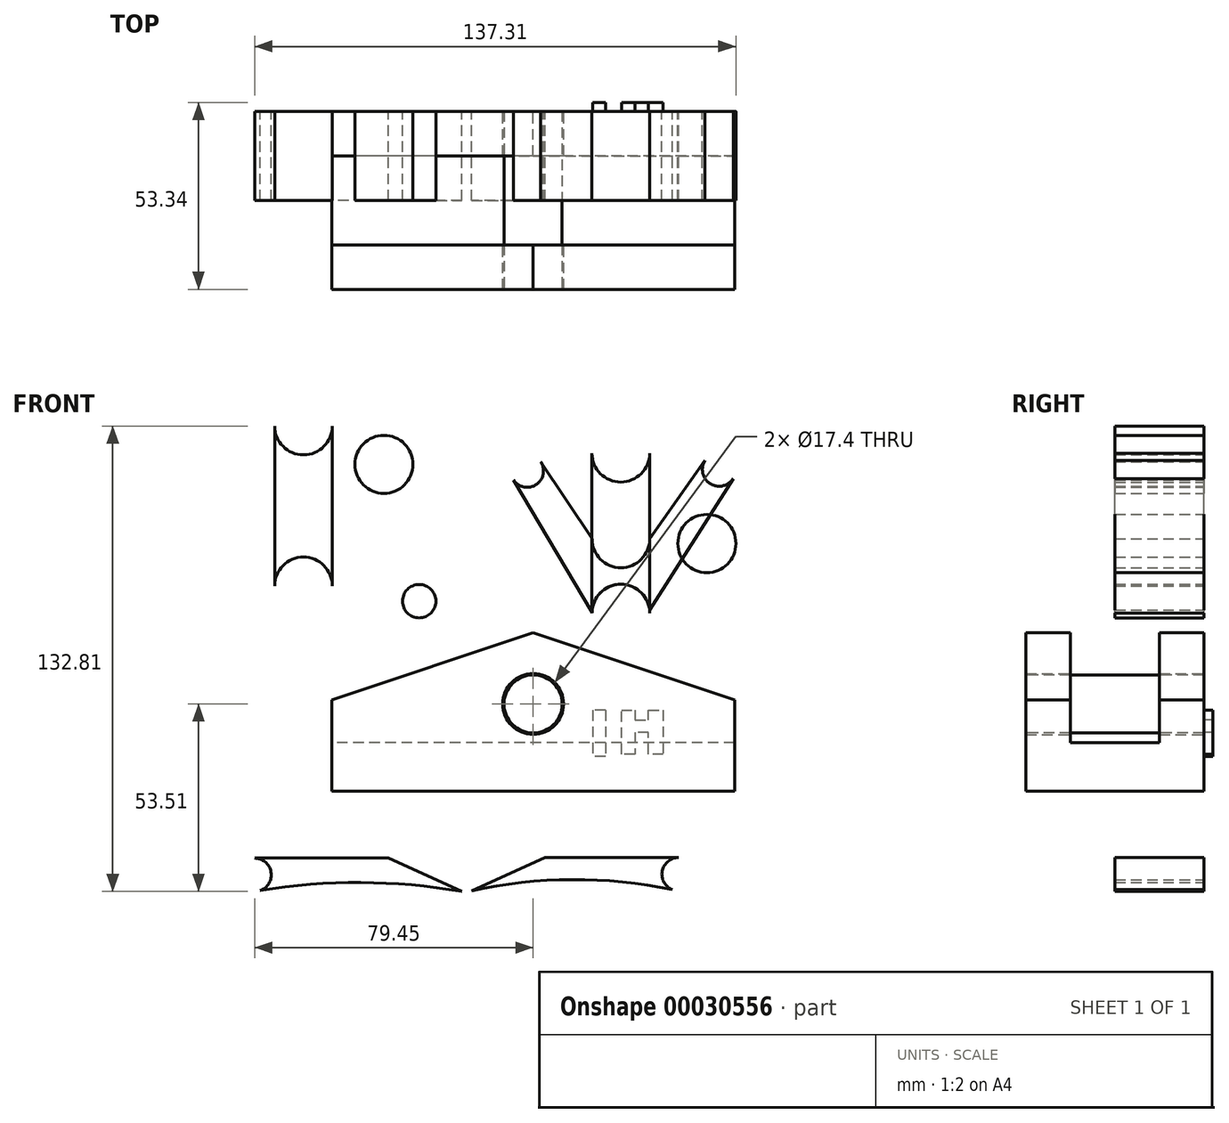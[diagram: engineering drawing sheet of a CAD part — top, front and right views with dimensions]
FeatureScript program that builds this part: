
annotation { "Feature Type Name" : "Feature", "Feature Type Description" : "" }
export const myFeature = defineFeature(function(context is Context, id is Id, definition is map)
    precondition{}
    {
        {
            var Q0;
            Q0=qCreatedBy(makeId("Front.planeOp"),FACE);
            var sketch = newSketch(context, id + "F0", { "sketchPlane" : qUnion([Q0])});
            skLineSegment(sketch, "E0", {"start": v(-48.02, -35.47) * mm, "end": v(66.9, -35.47) * mm});
            skLineSegment(sketch, "E1", {"start": v(66.9, -35.47) * mm, "end": v(66.9, -9.44) * mm});
            skLineSegment(sketch, "E2", {"start": v(-48.02, -35.47) * mm, "end": v(-48.02, -9.44) * mm});
            skLineSegment(sketch, "E3", {"start": v(9.44, 9.8) * mm, "end": v(-48.02, -9.44) * mm});
            skLineSegment(sketch, "E4", {"start": v(9.44, 9.8) * mm, "end": v(66.9, -9.44) * mm});
            skPoint(sketch, "E5.start.orphan", {"position": v(9.44, -35.47) * mm});
            skCircle(sketch, "E6", {"center": v(9.44, -10.54) * mm, "radius": 8.7 * mm});
            skSolve(sketch);
        }
        {
            var Q0;
            Q0=makeQuery(id+"F0.imprint","IMPRINT",FACE,{"disambiguationData":[TD([[makeQuery(id+"F0.imprint","IMPRINT",EDGE,{"derivedFrom":sQuery(id+"F0.wireOp",EDGE,"E0")}),1.0]])]});
            extrude(context, id + "F1", {"entities" : qUnion([Q0]), "depth" : 50.8 * mm});
        }
        {
            var Q0;
            Q0=makeQuery(id+"F1.opExtrude","SWEPT_FACE",FACE,{"disambiguationData":[OSD([sQuery(id+"F0.wireOp",EDGE,"E2")])]});
            var sketch = newSketch(context, id + "F2", { "sketchPlane" : qUnion([Q0])});
            skLineSegment(sketch, "E7", {"start": v(0, -9.44) * mm, "end": v(12.7, -9.44) * mm});
            skLineSegment(sketch, "E8", {"start": v(12.7, -9.44) * mm, "end": v(38.1, -9.44) * mm});
            skLineSegment(sketch, "E9", {"start": v(38.1, -9.44) * mm, "end": v(50.8, -9.44) * mm});
            skLineSegment(sketch, "E10", {"start": v(12.7, -9.44) * mm, "end": v(12.7, 15.96) * mm});
            skLineSegment(sketch, "E11", {"start": v(12.7, 15.96) * mm, "end": v(38.1, 15.96) * mm});
            skLineSegment(sketch, "E12", {"start": v(38.1, 15.96) * mm, "end": v(38.1, -9.44) * mm});
            skLineSegment(sketch, "E13", {"start": v(12.7, -9.44) * mm, "end": v(12.7, -21.58) * mm});
            skLineSegment(sketch, "E14", {"start": v(12.7, -21.58) * mm, "end": v(38.1, -21.58) * mm});
            skLineSegment(sketch, "E15", {"start": v(38.1, -21.58) * mm, "end": v(38.1, -9.44) * mm});
            skSolve(sketch);
        }
        {
            var Q0;
            Q0=makeQuery(id+"F2.imprint","IMPRINT",FACE,{"disambiguationData":[TD([[makeQuery(id+"F2.imprint","IMPRINT",EDGE,{"derivedFrom":sQuery(id+"F2.wireOp",EDGE,"E8")}),-1.0]])]});
            var Q1;
            Q1=makeQuery(id+"F2.imprint","IMPRINT",FACE,{"disambiguationData":[TD([[makeQuery(id+"F2.imprint","IMPRINT",EDGE,{"derivedFrom":sQuery(id+"F2.wireOp",EDGE,"E8")}),1.0]])]});
            extrude(context, id + "F3", {"entities" : qUnion([Q0, Q1]), "operationType" : NewBodyOperationType.REMOVE, "oppositeDirection" : true, "depth" : 228.6 * mm});
        }
        {
            var Q0;
            Q0=makeQuery(id+"F1.opExtrude","CAP_FACE",FACE,{"disambiguationData":[OSD([sQuery(id+"F0.wireOp",EDGE,"E0"),sQuery(id+"F0.wireOp",EDGE,"E1"),sQuery(id+"F0.wireOp",EDGE,"E2"),sQuery(id+"F0.wireOp",EDGE,"E3"),sQuery(id+"F0.wireOp",EDGE,"E4"),sQuery(id+"F0.wireOp",EDGE,"E6")])],"isStart":false});
            var sketch = newSketch(context, id + "F4", { "sketchPlane" : qUnion([Q0])});
            skCircle(sketch, "E16", {"center": v(9.44, -10.54) * mm, "radius": 8.29 * mm});
            skSolve(sketch);
        }
        {
            var Q0;
            Q0=makeQuery(id+"F4.imprint","IMPRINT",FACE,{"disambiguationData":[TD([[makeQuery(id+"F4.imprint","IMPRINT",EDGE,{"derivedFrom":sQuery(id+"F4.wireOp",EDGE,"E16")}),1.0]])]});
            extrude(context, id + "F5", {"entities" : qUnion([Q0]), "oppositeDirection" : true, "depth" : 50.8 * mm});
        }
        {
            var Q0;
            Q0=qCreatedBy(makeId("Front.planeOp"),FACE);
            var sketch = newSketch(context, id + "F6", { "sketchPlane" : qUnion([Q0])});
            skLineSegment(sketch, "E17", {"start": v(26.22, 15.37) * mm, "end": v(26.22, 61) * mm});
            skLineSegment(sketch, "E18", {"start": v(42.7, 15.37) * mm, "end": v(42.7, 61) * mm});
            skArc(sketch, "E19", {"start": v(42.7, 15.37) * mm, "mid": v(34.46, 23.61) * mm, "end": v(26.22, 15.37) * mm});
            skArc(sketch, "E20", {"start": v(26.22, 61) * mm, "mid": v(34.46, 52.77) * mm, "end": v(42.7, 61) * mm});
            skSolve(sketch);
        }
        {
            var Q0;
            Q0=makeQuery(id+"F6.imprint","IMPRINT",FACE,{"disambiguationData":[TD([[makeQuery(id+"F6.imprint","IMPRINT",EDGE,{"derivedFrom":sQuery(id+"F6.wireOp",EDGE,"E17")}),-1.0]])]});
            var Q1;
            Q1=sQuery(id+"F6.wireOp",EDGE,"E17");
            var Q2;
            Q2=sQuery(id+"F6.wireOp",EDGE,"E18");
            var Q3;
            Q3=sQuery(id+"F6.wireOp",EDGE,"dfab5041-fabf-45aa-a716-34bc4bf7221b");
            var Q4;
            Q4=sQuery(id+"F6.wireOp",EDGE,"E19");
            extrude(context, id + "F7", {"entities" : qUnion([Q0]), "surfaceEntities" : qUnion([Q1, Q2, Q3, Q4]), "depth" : 25.4 * mm});
        }
        {
            var Q0;
            Q0=qCreatedBy(makeId("Front.planeOp"),FACE);
            var sketch = newSketch(context, id + "F8", { "sketchPlane" : qUnion([Q0])});
            skCircle(sketch, "E21", {"center": v(59.02, 35.23) * mm, "radius": 8.29 * mm});
            skSolve(sketch);
        }
        {
            var Q0;
            Q0=makeQuery(id+"F8.imprint","IMPRINT",FACE,{"disambiguationData":[TD([[makeQuery(id+"F8.imprint","IMPRINT",EDGE,{"derivedFrom":sQuery(id+"F8.wireOp",EDGE,"E21")}),1.0]])]});
            extrude(context, id + "F9", {"entities" : qUnion([Q0]), "depth" : 25.4 * mm});
        }
        {
            var Q0;
            Q0=qCreatedBy(makeId("Front.planeOp"),FACE);
            var sketch = newSketch(context, id + "F10", { "sketchPlane" : qUnion([Q0])});
            skLineSegment(sketch, "E22", {"start": v(-64.3, 23.13) * mm, "end": v(-64.3, 68.76) * mm});
            skLineSegment(sketch, "E23", {"start": v(-47.83, 23.13) * mm, "end": v(-47.83, 68.76) * mm});
            skArc(sketch, "E24", {"start": v(-47.83, 23.13) * mm, "mid": v(-56.06, 31.37) * mm, "end": v(-64.3, 23.13) * mm});
            skArc(sketch, "E25", {"start": v(-64.3, 68.76) * mm, "mid": v(-56.06, 60.53) * mm, "end": v(-47.83, 68.76) * mm});
            skSolve(sketch);
        }
        {
            var Q0;
            Q0=makeQuery(id+"F10.imprint","IMPRINT",FACE,{"disambiguationData":[TD([[makeQuery(id+"F10.imprint","IMPRINT",EDGE,{"derivedFrom":sQuery(id+"F10.wireOp",EDGE,"E22")}),-1.0]])]});
            var Q1;
            Q1=sQuery(id+"F10.wireOp",EDGE,"E22");
            var Q2;
            Q2=sQuery(id+"F10.wireOp",EDGE,"E23");
            var Q3;
            Q3=sQuery(id+"F10.wireOp",EDGE,"E24");
            var Q4;
            Q4=sQuery(id+"F10.wireOp",EDGE,"E25");
            extrude(context, id + "F11", {"entities" : qUnion([Q0]), "surfaceEntities" : qUnion([Q1, Q2, Q3, Q4]), "depth" : 25.4 * mm});
        }
        {
            var Q0;
            Q0=qCreatedBy(makeId("Front.planeOp"),FACE);
            var sketch = newSketch(context, id + "F12", { "sketchPlane" : qUnion([Q0])});
            skCircle(sketch, "E26", {"center": v(-33.11, 57.82) * mm, "radius": 8.29 * mm});
            skSolve(sketch);
        }
        {
            var Q0;
            Q0=makeQuery(id+"F12.imprint","IMPRINT",FACE,{"disambiguationData":[TD([[makeQuery(id+"F12.imprint","IMPRINT",EDGE,{"derivedFrom":sQuery(id+"F12.wireOp",EDGE,"E26")}),1.0]])]});
            var Q1;
            Q1=sQuery(id+"F12.wireOp",EDGE,"E26");
            extrude(context, id + "F13", {"entities" : qUnion([Q0]), "surfaceEntities" : qUnion([Q1]), "depth" : 25.4 * mm});
        }
        {
            var Q0;
            Q0=qCreatedBy(makeId("Front.planeOp"),FACE);
            var sketch = newSketch(context, id + "F14", { "sketchPlane" : qUnion([Q0])});
            skArc(sketch, "E27", {"start": v(42.65, 16.26) * mm, "mid": v(34.1, 23.59) * mm, "end": v(26.25, 15.52) * mm});
            skLineSegment(sketch, "E28", {"start": v(42.65, 16.26) * mm, "end": v(66.5, 53.77) * mm});
            skLineSegment(sketch, "E29", {"start": v(26.25, 15.52) * mm, "end": v(3.61, 53.77) * mm});
            skArc(sketch, "E30", {"start": v(26.24, 36.57) * mm, "mid": v(34.47, 28.34) * mm, "end": v(42.7, 36.57) * mm});
            skLineSegment(sketch, "E31", {"start": v(42.7, 36.57) * mm, "end": v(58.47, 58.88) * mm});
            skLineSegment(sketch, "E32", {"start": v(26.24, 36.57) * mm, "end": v(11.61, 58.5) * mm});
            skArc(sketch, "E33", {"start": v(58.47, 58.88) * mm, "mid": v(59.93, 52.3) * mm, "end": v(66.5, 53.77) * mm});
            skArc(sketch, "E34", {"start": v(3.61, 53.77) * mm, "mid": v(10.11, 51.91) * mm, "end": v(11.61, 58.5) * mm});
            skSolve(sketch);
        }
        {
            var Q0;
            Q0=makeQuery(id+"F14.imprint","IMPRINT",FACE,{"disambiguationData":[TD([[makeQuery(id+"F14.imprint","IMPRINT",EDGE,{"derivedFrom":sQuery(id+"F14.wireOp",EDGE,"E27")}),-1.0]])]});
            extrude(context, id + "F15", {"entities" : qUnion([Q0]), "depth" : 25.4 * mm});
        }
        {
            var Q0;
            Q0=qCreatedBy(makeId("Front.planeOp"),FACE);
            var sketch = newSketch(context, id + "F16", { "sketchPlane" : qUnion([Q0])});
            skCircle(sketch, "E35", {"center": v(-23.05, 18.79) * mm, "radius": 4.76 * mm});
            skSolve(sketch);
        }
        {
            var Q0;
            Q0=makeQuery(id+"F16.imprint","IMPRINT",FACE,{"disambiguationData":[TD([[makeQuery(id+"F16.imprint","IMPRINT",EDGE,{"derivedFrom":sQuery(id+"F16.wireOp",EDGE,"E35")}),1.0]])]});
            extrude(context, id + "F17", {"entities" : qUnion([Q0]), "depth" : 25.4 * mm});
        }
        {
            var Q0;
            Q0=qCreatedBy(makeId("Front.planeOp"),FACE);
            var sketch = newSketch(context, id + "F18", { "sketchPlane" : qUnion([Q0])});
            skArc(sketch, "E36", {"start": v(50.94, -54.35) * mm, "mid": v(46.18, -59) * mm, "end": v(50.72, -63.87) * mm});
            skLineSegment(sketch, "E37", {"start": v(50.94, -54.35) * mm, "end": v(12.84, -54.35) * mm});
            skLineSegment(sketch, "E38", {"start": v(-8.12, -63.87) * mm, "end": v(12.84, -54.35) * mm});
            skArc(sketch, "E39", {"start": v(50.72, -63.87) * mm, "mid": v(21.3, -60.65) * mm, "end": v(-8.12, -63.87) * mm});
            skSolve(sketch);
        }
        {
            var Q0;
            {var subQ4=sQuery(id+"F18.wireOp",EDGE,"E37");Q0=makeQuery(id+"F18.imprint","IMPRINT",FACE,{"disambiguationData":[TD([[makeQuery(id+"F18.imprint","IMPRINT",EDGE,{"derivedFrom":subQ4}),1.0]])]});}
            extrude(context, id + "F19", {"entities" : qUnion([Q0]), "depth" : 25.4 * mm});
        }
        {
            var Q0;
            Q0=qCreatedBy(makeId("Front.planeOp"),FACE);
            var sketch = newSketch(context, id + "F20", { "sketchPlane" : qUnion([Q0])});
            skArc(sketch, "E40", {"start": v(-70.01, -64.06) * mm, "mid": v(-65.25, -59.3) * mm, "end": v(-70.01, -54.53) * mm});
            skLineSegment(sketch, "E41", {"start": v(-70.01, -54.53) * mm, "end": v(-31.91, -54.53) * mm});
            skLineSegment(sketch, "E42", {"start": v(-31.91, -54.53) * mm, "end": v(-10.96, -64.05) * mm});
            skLineSegment(sketch, "E43", {"start": v(-70.01, -59.3) * mm, "end": v(-65.25, -59.3) * mm});
            skArc(sketch, "E44", {"start": v(-10.96, -64.05) * mm, "mid": v(-40.49, -61.48) * mm, "end": v(-70.01, -64.06) * mm});
            skSolve(sketch);
        }
        {
            var Q0;
            {var subQ4=sQuery(id+"F20.wireOp",EDGE,"E41");Q0=makeQuery(id+"F20.imprint","IMPRINT",FACE,{"disambiguationData":[TD([[makeQuery(id+"F20.imprint","IMPRINT",EDGE,{"derivedFrom":subQ4}),-1.0]])]});}
            extrude(context, id + "F21", {"entities" : qUnion([Q0]), "depth" : 25.4 * mm});
        }
        {
            var Q0;
            Q0=makeQuery(id+"F1.opExtrude","CAP_FACE",FACE,{"disambiguationData":[OSD([sQuery(id+"F0.wireOp",EDGE,"E0"),sQuery(id+"F0.wireOp",EDGE,"E1"),sQuery(id+"F0.wireOp",EDGE,"E2"),sQuery(id+"F0.wireOp",EDGE,"E3"),sQuery(id+"F0.wireOp",EDGE,"E4"),sQuery(id+"F0.wireOp",EDGE,"E6")])],"isStart":true});
            var sketch = newSketch(context, id + "F22", { "sketchPlane" : qUnion([Q0])});
            skLineSegment(sketch, "E45", {"start": v(-46.56, -12.37) * mm, "end": v(-46.56, -24.84) * mm});
            skLineSegment(sketch, "E46", {"start": v(-46.56, -24.84) * mm, "end": v(-42.34, -24.84) * mm});
            skLineSegment(sketch, "E47", {"start": v(-42.34, -24.84) * mm, "end": v(-42.34, -18.6) * mm});
            skLineSegment(sketch, "E48", {"start": v(-42.34, -18.6) * mm, "end": v(-38.5, -18.6) * mm});
            skLineSegment(sketch, "E49", {"start": v(-38.5, -18.6) * mm, "end": v(-38.5, -24.84) * mm});
            skLineSegment(sketch, "E50", {"start": v(-38.5, -24.84) * mm, "end": v(-34.64, -24.84) * mm});
            skLineSegment(sketch, "E51", {"start": v(-34.64, -24.84) * mm, "end": v(-34.64, -12.37) * mm});
            skLineSegment(sketch, "E52", {"start": v(-34.64, -12.37) * mm, "end": v(-38.5, -12.37) * mm});
            skLineSegment(sketch, "E53", {"start": v(-38.5, -12.37) * mm, "end": v(-38.5, -15.12) * mm});
            skLineSegment(sketch, "E54", {"start": v(-38.5, -15.12) * mm, "end": v(-42.34, -15.12) * mm});
            skLineSegment(sketch, "E55", {"start": v(-42.34, -15.12) * mm, "end": v(-42.34, -12.37) * mm});
            skLineSegment(sketch, "E56", {"start": v(-42.34, -12.37) * mm, "end": v(-46.56, -12.37) * mm});
            skLineSegment(sketch, "E57", {"start": v(-30.06, -12.37) * mm, "end": v(-30.06, -25.57) * mm});
            skLineSegment(sketch, "E58", {"start": v(-30.06, -25.57) * mm, "end": v(-26.4, -25.57) * mm});
            skLineSegment(sketch, "E59", {"start": v(-30.06, -12.37) * mm, "end": v(-26.4, -12.37) * mm});
            skLineSegment(sketch, "E60", {"start": v(-26.4, -12.37) * mm, "end": v(-26.4, -25.57) * mm});
            skSolve(sketch);
        }
        {
            var Q0;
            Q0=makeQuery(id+"F22.imprint","IMPRINT",FACE,{"disambiguationData":[TD([[makeQuery(id+"F22.imprint","IMPRINT",EDGE,{"derivedFrom":sQuery(id+"F22.wireOp",EDGE,"E45")}),1.0]])]});
            var Q1;
            Q1=makeQuery(id+"F22.imprint","IMPRINT",FACE,{"disambiguationData":[TD([[makeQuery(id+"F22.imprint","IMPRINT",EDGE,{"derivedFrom":sQuery(id+"F22.wireOp",EDGE,"E57")}),1.0]])]});
            extrude(context, id + "F23", {"entities" : qUnion([Q0, Q1]), "operationType" : NewBodyOperationType.ADD, "depth" : 2.54 * mm});
        }
    });
